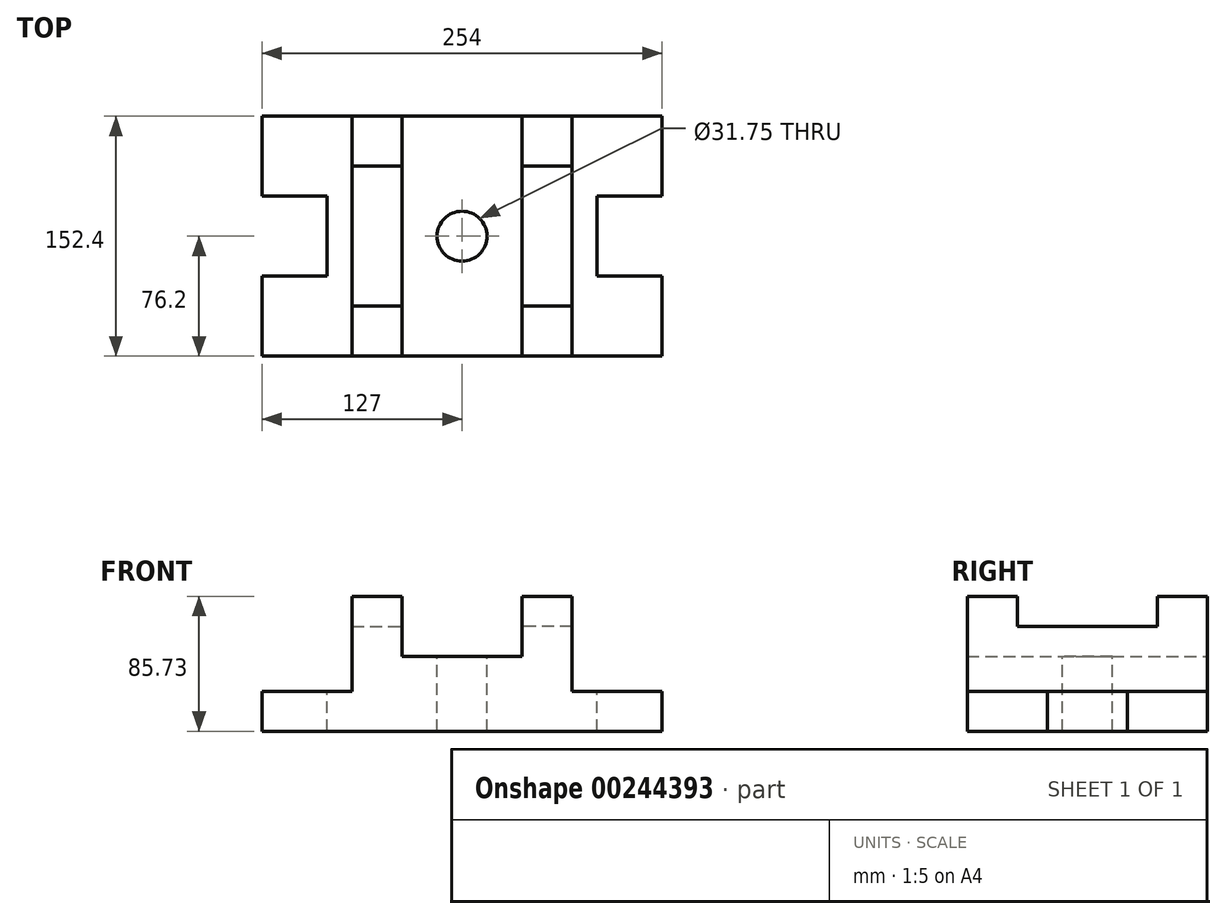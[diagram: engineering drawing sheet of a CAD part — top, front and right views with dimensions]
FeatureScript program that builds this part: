
annotation { "Feature Type Name" : "Feature", "Feature Type Description" : "" }
export const myFeature = defineFeature(function(context is Context, id is Id, definition is map)
    precondition{}
    {
        {
            var Q0;
            Q0=qCreatedBy(makeId("Front.planeOp"),FACE);
            var sketch = newSketch(context, id + "F0", { "sketchPlane" : qUnion([Q0])});
            skLineSegment(sketch, "E0.bottom", {"start": v(-38.1, 53.98) * mm, "end": v(38.1, 53.98) * mm});
            skLineSegment(sketch, "E0.top", {"start": v(-69.85, 31.75) * mm, "end": v(69.85, 31.75) * mm});
            skLineSegment(sketch, "E0.left", {"start": v(-69.85, 53.98) * mm, "end": v(-69.85, 31.75) * mm});
            skLineSegment(sketch, "E0.right", {"start": v(69.85, 53.98) * mm, "end": v(69.85, 31.75) * mm});
            skLineSegment(sketch, "E1.bottom", {"start": v(-69.85, 73.03) * mm, "end": v(-38.1, 73.03) * mm});
            skLineSegment(sketch, "E1.left", {"start": v(-69.85, 73.03) * mm, "end": v(-69.85, 53.98) * mm});
            skLineSegment(sketch, "E1.right", {"start": v(-38.1, 73.03) * mm, "end": v(-38.1, 53.98) * mm});
            skLineSegment(sketch, "E2.bottom", {"start": v(38.1, 73.03) * mm, "end": v(69.85, 73.03) * mm});
            skLineSegment(sketch, "E2.left", {"start": v(38.1, 73.03) * mm, "end": v(38.1, 53.98) * mm});
            skLineSegment(sketch, "E2.right", {"start": v(69.85, 73.03) * mm, "end": v(69.85, 53.98) * mm});
            skSolve(sketch);
        }
        {
            var Q0;
            Q0=makeQuery(id+"F0.imprint","IMPRINT",FACE,{"disambiguationData":[TD([[makeQuery(id+"F0.imprint","IMPRINT",EDGE,{"derivedFrom":sQuery(id+"F0.wireOp",EDGE,"E0.bottom")}),-1.0]])]});
            extrude(context, id + "F1", {"entities" : qUnion([Q0]), "endBound" : BoundingType.SYMMETRIC, "depth" : 152.4 * mm});
        }
        {
            var Q0;
            Q0=makeQuery(id+"F1.opExtrude","SWEPT_FACE",FACE,{"disambiguationData":[OSD([sQuery(id+"F0.wireOp",EDGE,"E2.bottom")])]});
            var sketch = newSketch(context, id + "F2", { "sketchPlane" : qUnion([Q0])});
            skLineSegment(sketch, "E3.bottom", {"start": v(38.1, 76.2) * mm, "end": v(69.85, 76.2) * mm});
            skLineSegment(sketch, "E3.top", {"start": v(38.1, 44.45) * mm, "end": v(69.85, 44.45) * mm});
            skLineSegment(sketch, "E3.left", {"start": v(38.1, 76.2) * mm, "end": v(38.1, 44.45) * mm});
            skLineSegment(sketch, "E3.right", {"start": v(69.85, 76.2) * mm, "end": v(69.85, 44.45) * mm});
            skLineSegment(sketch, "E4.bottom", {"start": v(69.85, -76.2) * mm, "end": v(38.1, -76.2) * mm});
            skLineSegment(sketch, "E4.top", {"start": v(69.85, -44.45) * mm, "end": v(38.1, -44.45) * mm});
            skLineSegment(sketch, "E4.left", {"start": v(69.85, -76.2) * mm, "end": v(69.85, -44.45) * mm});
            skLineSegment(sketch, "E4.right", {"start": v(38.1, -76.2) * mm, "end": v(38.1, -44.45) * mm});
            skLineSegment(sketch, "E5.bottom", {"start": v(-69.85, 76.2) * mm, "end": v(-38.1, 76.2) * mm});
            skLineSegment(sketch, "E5.top", {"start": v(-69.85, 44.45) * mm, "end": v(-38.1, 44.45) * mm});
            skLineSegment(sketch, "E5.left", {"start": v(-69.85, 76.2) * mm, "end": v(-69.85, 44.45) * mm});
            skLineSegment(sketch, "E5.right", {"start": v(-38.1, 76.2) * mm, "end": v(-38.1, 44.45) * mm});
            skLineSegment(sketch, "E6.bottom", {"start": v(-69.85, -76.2) * mm, "end": v(-38.1, -76.2) * mm});
            skLineSegment(sketch, "E6.top", {"start": v(-69.85, -44.45) * mm, "end": v(-38.1, -44.45) * mm});
            skLineSegment(sketch, "E6.left", {"start": v(-69.85, -76.2) * mm, "end": v(-69.85, -44.45) * mm});
            skLineSegment(sketch, "E6.right", {"start": v(-38.1, -76.2) * mm, "end": v(-38.1, -44.45) * mm});
            skSolve(sketch);
        }
        {
            var Q0;
            Q0 = qSketchRegion(id + "F2", true);
            extrude(context, id + "F3", {"entities" : qUnion([Q0]), "operationType" : NewBodyOperationType.ADD, "depth" : 19.05 * mm});
        }
        {
            var Q0;
            Q0=makeQuery(id+"F1.opExtrude","SWEPT_FACE",FACE,{"disambiguationData":[OSD([sQuery(id+"F0.wireOp",EDGE,"E0.bottom")])]});
            var sketch = newSketch(context, id + "F4", { "sketchPlane" : qUnion([Q0])});
            skCircle(sketch, "E7", {"center": v(0, 0) * mm, "radius": 15.88 * mm});
            skSolve(sketch);
        }
        {
            var Q0;
            Q0=makeQuery(id+"F4.imprint","IMPRINT",FACE,{"disambiguationData":[TD([[makeQuery(id+"F4.imprint","IMPRINT",EDGE,{"derivedFrom":sQuery(id+"F4.wireOp",EDGE,"E7")}),1.0]])]});
            extrude(context, id + "F5", {"entities" : qUnion([Q0]), "operationType" : NewBodyOperationType.REMOVE, "oppositeDirection" : true, "depth" : 25.4 * mm});
        }
        {
            var Q0;
            Q0=makeQuery(id+"F1.opExtrude","SWEPT_FACE",FACE,{"disambiguationData":[OSD([sQuery(id+"F0.wireOp",EDGE,"E0.top")])]});
            var sketch = newSketch(context, id + "F6", { "sketchPlane" : qUnion([Q0])});
            skLineSegment(sketch, "E8.bottom", {"start": v(-127, 76.2) * mm, "end": v(127, 76.2) * mm});
            skLineSegment(sketch, "E8.top", {"start": v(-127, 25.4) * mm, "end": v(127, 25.4) * mm});
            skLineSegment(sketch, "E8.left", {"start": v(-127, 76.2) * mm, "end": v(-127, 25.4) * mm});
            skLineSegment(sketch, "E8.right", {"start": v(127, 76.2) * mm, "end": v(127, 25.4) * mm});
            skLineSegment(sketch, "E9.bottom", {"start": v(-127, -25.4) * mm, "end": v(127, -25.4) * mm});
            skLineSegment(sketch, "E9.top", {"start": v(-127, -76.2) * mm, "end": v(127, -76.2) * mm});
            skLineSegment(sketch, "E9.left", {"start": v(-127, -25.4) * mm, "end": v(-127, -76.2) * mm});
            skLineSegment(sketch, "E9.right", {"start": v(127, -25.4) * mm, "end": v(127, -76.2) * mm});
            skLineSegment(sketch, "E10.bottom", {"start": v(-85.73, 25.4) * mm, "end": v(85.72, 25.4) * mm});
            skLineSegment(sketch, "E10.top", {"start": v(-85.73, -25.4) * mm, "end": v(85.72, -25.4) * mm});
            skLineSegment(sketch, "E10.left", {"start": v(-85.73, 25.4) * mm, "end": v(-85.73, -25.4) * mm});
            skLineSegment(sketch, "E10.right", {"start": v(85.72, 25.4) * mm, "end": v(85.72, -25.4) * mm});
            skCircle(sketch, "E11", {"center": v(0, 0) * mm, "radius": 15.88 * mm});
            skSolve(sketch);
        }
        {
            var Q0;
            Q0 = qSketchRegion(id + "F6", true);
            extrude(context, id + "F7", {"entities" : qUnion([Q0]), "operationType" : NewBodyOperationType.ADD, "depth" : 25.4 * mm});
        }
    });
